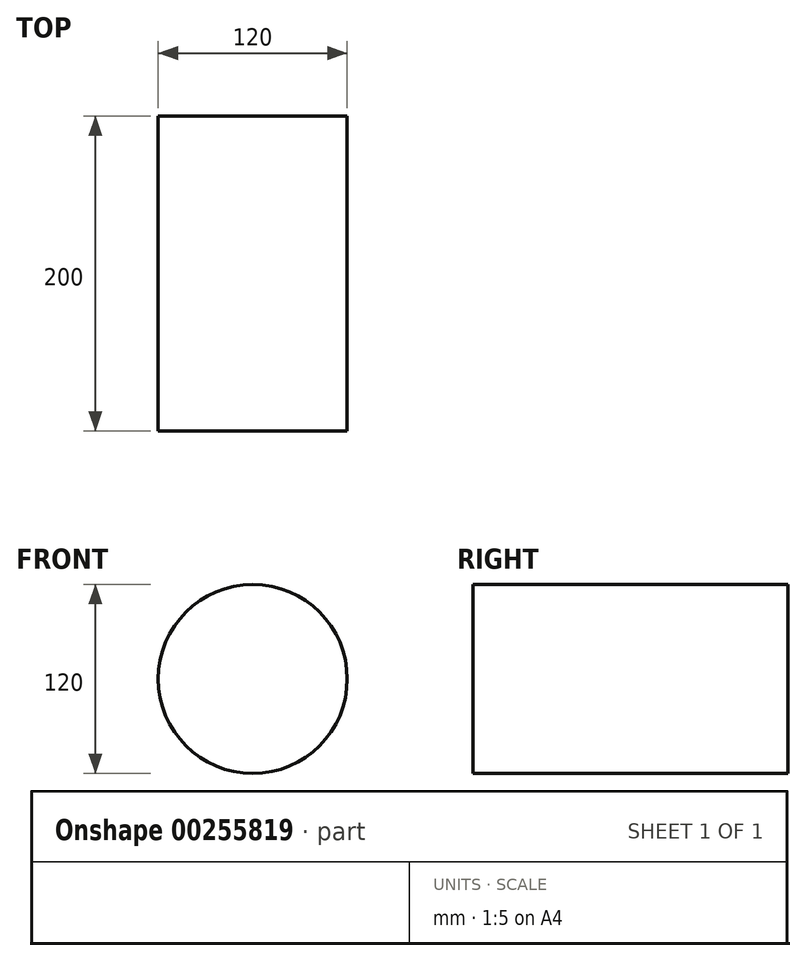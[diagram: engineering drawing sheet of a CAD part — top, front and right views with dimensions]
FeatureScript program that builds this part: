
annotation { "Feature Type Name" : "Feature", "Feature Type Description" : "" }
export const myFeature = defineFeature(function(context is Context, id is Id, definition is map)
    precondition{}
    {
        {
            var Q0;
            Q0=qCreatedBy(makeId("Front.planeOp"),FACE);
            var sketch = newSketch(context, id + "F0", { "sketchPlane" : qUnion([Q0])});
            skCircle(sketch, "E0", {"center": v(0, 0) * mm, "radius": 60 * mm});
            skSolve(sketch);
        }
        {
            var Q0;
            Q0 = qSketchRegion(id + "F0", true);
            extrude(context, id + "F1", {"entities" : qUnion([Q0]), "oppositeDirection" : true, "depth" : 200 * mm, "offsetDistance" : 25 * mm});
        }
    });
